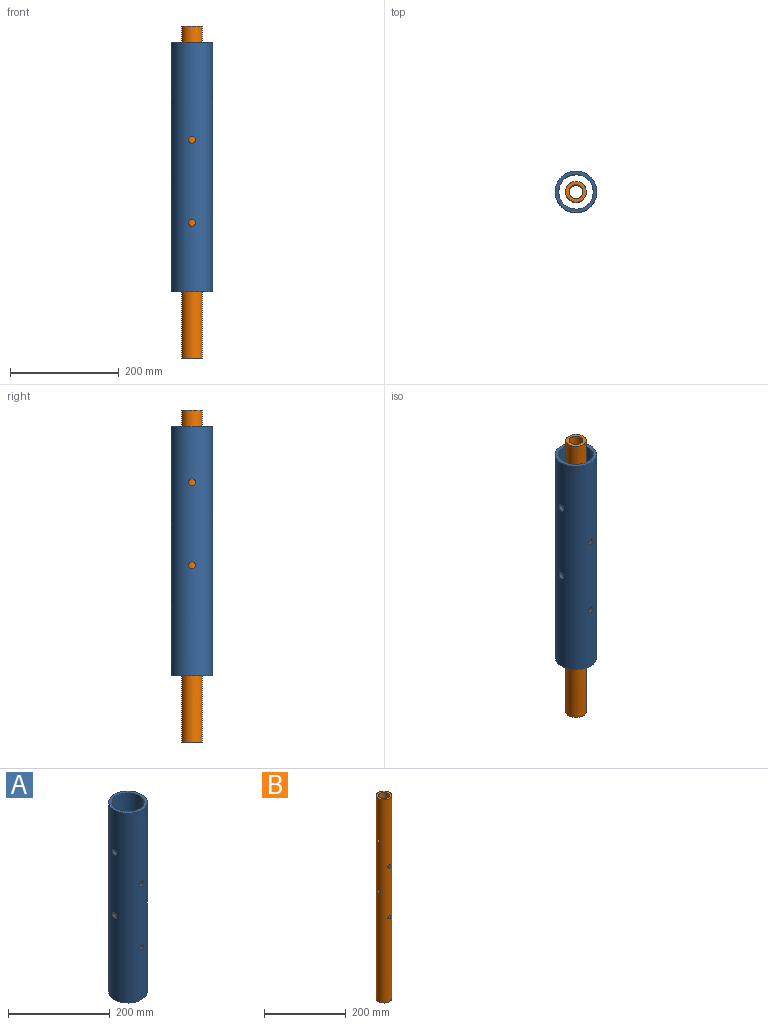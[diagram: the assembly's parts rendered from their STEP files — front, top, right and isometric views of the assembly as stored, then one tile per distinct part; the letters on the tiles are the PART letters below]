
ASSEMBLY  parts=2 mates=1
PART A: 12 faces, bbox 76.2x76.2x457.2 mm
  f0: cylinder r=31.75mm len=457.2mm, axis (0,0,-1), area 90185.4mm2, adj f2,f3,f4,f5,f6,f7,f8,f9
  f1: cylinder r=38.1mm len=457.2mm, axis (0,0,-1), area 108427.9mm2, adj f2,f3,f4,f5,f6,f7,f8,f9
  f2: plane 76.2x76.2mm, normal (0,0,1), area 1393.4mm2, adj f0,f1
  f3: plane 76.2x76.2mm, normal (0,0,-1), area 1393.4mm2, adj f0,f1
  f4: cylinder r=6.35mm len=12.7mm, axis (0,-1,0), area 255.5mm2, adj f0,f1
  f5: cylinder r=6.35mm len=12.7mm, axis (0,-1,0), area 255.5mm2, adj f0,f1
  f6: cylinder r=6.35mm len=12.7mm, axis (0,-1,0), area 255.5mm2, adj f0,f1
  f7: cylinder r=6.35mm len=12.7mm, axis (0,-1,0), area 255.5mm2, adj f0,f1
  f8: cylinder r=6.35mm len=12.7mm, axis (-1,0,0), area 255.5mm2, adj f0,f1
  f9: cylinder r=6.35mm len=12.7mm, axis (-1,0,0), area 255.5mm2, adj f0,f1
  f10: cylinder r=6.35mm len=12.7mm, axis (-1,0,0), area 255.5mm2, adj f0,f1
  f11: cylinder r=6.35mm len=12.7mm, axis (-1,0,0), area 255.5mm2, adj f0,f1
PART B: 12 faces, bbox 38.1x38.1x609.6 mm
  f0: cylinder r=12.7mm len=609.6mm, axis (0,0,-1), area 48064mm2, adj f2,f3,f4,f5,f6,f7,f8,f9
  f1: cylinder r=19.05mm len=609.6mm, axis (0,0,-1), area 72390.5mm2, adj f2,f3,f4,f5,f6,f7,f8,f9
  f2: plane 38.1x38.1mm, normal (0,0,1), area 633.4mm2, adj f0,f1
  f3: plane 38.1x38.1mm, normal (0,0,-1), area 633.4mm2, adj f0,f1
  f4: cylinder r=4.76mm len=9.53mm, axis (0,-1,0), area 194.8mm2, adj f0,f1
  f5: cylinder r=4.76mm len=9.53mm, axis (0,-1,0), area 194.7mm2, adj f0,f1
  f6: cylinder r=4.76mm len=9.53mm, axis (0,-1,0), area 194.8mm2, adj f0,f1
  f7: cylinder r=4.76mm len=9.53mm, axis (0,-1,0), area 194.7mm2, adj f0,f1
  f8: cylinder r=4.76mm len=9.53mm, axis (-1,0,0), area 194.7mm2, adj f0,f1
  f9: cylinder r=4.76mm len=9.53mm, axis (-1,0,0), area 194.7mm2, adj f0,f1
  f10: cylinder r=4.76mm len=9.53mm, axis (-1,0,0), area 194.7mm2, adj f0,f1
  f11: cylinder r=4.76mm len=9.53mm, axis (-1,0,0), area 194.7mm2, adj f0,f1
PLACE A at identity fixed
PLACE B rot(axis=(0,0,1),30.8deg) t=(0,0,-121.29)mm
MATE cylindrical B.f1 <-> A.f0  axis (0,0,-1) through (0,0,183.51)mm
